# Revit family: Lighting_Fixture-Ceiling-Astro-Vetro_Squarexxx
name_source: partatom
category: Lighting Fixtures
revit_build: Autodesk Revit LT 2014 (Build: 20130308_1515(x64)
units: mm (PartAtom-declared; Revit-internal decimal feet)

## types (1)
- 5668 Vetro Square
    Apparent Load = 12 VA
    Assembly Code = D5020200
    Casing Material = Astro - Aluminium - White
    Class = 3
    Color Filter = 16777215
    Default Elevation = 1219.2 mm  [stored 4 ft]
    Description = Downlight
    Dimmable = Yes
    Dimming Lamp Color Temperature Shift = <None>
    IP Rating = IP65
    Lamp = LED
    Lamp included = Yes
    Length = 90 mm  [stored 0.295276 ft]
    Luminaire Lamp Efficiency Rating = -A
    Manufacturer = Astro Lighting Ltd, CM20 2DP
    Model = 5668 Vetro Square
    Mountable on normally flammable surfaces = Yes
    Number of Poles = 1
    Photometric Web File = 5668 VETRO SINGLE SQUARE.ies
    Product Documentation = http://www.astrolighting.co.uk
    Suitable for bathroom zone = Zones 1, 2 and 3
    Tilt Angle = 90.00°
    Type Comments = Dimmable if a dimmable driver is used. Cutout size to fit: 80mm diameter. Leave 150mm void around the product. Not suitable for covering with insulation. Requires a 350mA constant current driver, not included.
    URL = www.astrolighting.co.uk
    Voltage = 230 V
    Wattage Comments = 10w
    Weight = 0.4kg
    Width = 90 mm  [stored 0.295276 ft]

note: [stored X ft] marks values corroborated as IEEE doubles in the binary element streams (Revit-internal decimal feet)

## geometry (parser evidence)
native form markers: Sweep x1
no freeform markers — native parametric forms only
